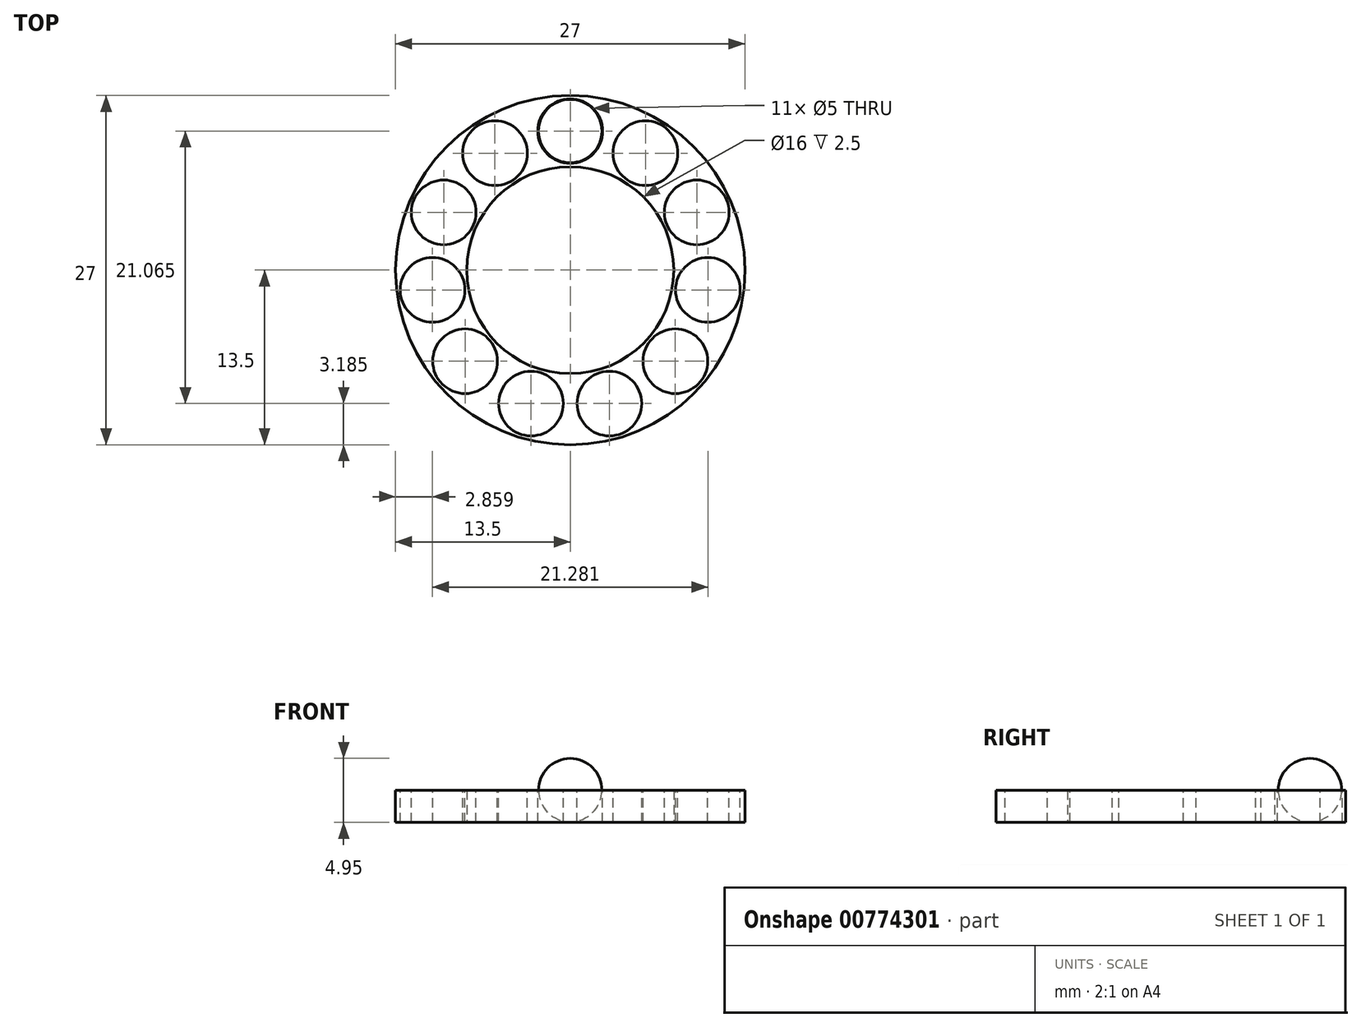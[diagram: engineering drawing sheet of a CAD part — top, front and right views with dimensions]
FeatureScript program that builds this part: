
annotation { "Feature Type Name" : "Feature", "Feature Type Description" : "" }
export const myFeature = defineFeature(function(context is Context, id is Id, definition is map)
    precondition{}
    {
        {
            var Q0;
            Q0=qCreatedBy(makeId("Top.planeOp"),FACE);
            var sketch = newSketch(context, id + "F0", { "sketchPlane" : qUnion([Q0])});
            skCircle(sketch, "E0", {"center": v(0, 0) * mm, "radius": 8 * mm});
            skCircle(sketch, "E1", {"center": v(0, 0) * mm, "radius": 13.5 * mm});
            skSolve(sketch);
        }
        {
            var Q0;
            Q0 = qSketchRegion(id + "F0", true);
            extrude(context, id + "F1", {"entities" : qUnion([Q0]), "depth" : 2.5 * mm, "offsetDistance" : 25 * mm});
        }
        {
            var Q0;
            Q0=makeQuery(id+"F1.opExtrude","CAP_FACE",FACE,{"disambiguationData":[OSD([sQuery(id+"F0.wireOp",EDGE,"E0"),sQuery(id+"F0.wireOp",EDGE,"E1")])],"isStart":false});
            var sketch = newSketch(context, id + "F2", { "sketchPlane" : qUnion([Q0])});
            skCircle(sketch, "E2", {"center": v(0, 10.75) * mm, "radius": 2.5 * mm});
            skCircle(sketch, "E3.1.0", {"center": v(5.81, 9.04) * mm, "radius": 2.5 * mm});
            skCircle(sketch, "E3.2.0", {"center": v(9.78, 4.47) * mm, "radius": 2.5 * mm});
            skCircle(sketch, "E3.3.0", {"center": v(10.64, -1.53) * mm, "radius": 2.5 * mm});
            skCircle(sketch, "E3.4.0", {"center": v(8.12, -7.04) * mm, "radius": 2.5 * mm});
            skCircle(sketch, "E3.5.0", {"center": v(3.03, -10.31) * mm, "radius": 2.5 * mm});
            skCircle(sketch, "E3.6.0", {"center": v(-3.03, -10.31) * mm, "radius": 2.5 * mm});
            skCircle(sketch, "E3.7.0", {"center": v(-8.12, -7.04) * mm, "radius": 2.5 * mm});
            skCircle(sketch, "E3.8.0", {"center": v(-10.64, -1.53) * mm, "radius": 2.5 * mm});
            skCircle(sketch, "E3.9.0", {"center": v(-9.78, 4.47) * mm, "radius": 2.5 * mm});
            skCircle(sketch, "E3.10.0", {"center": v(-5.81, 9.04) * mm, "radius": 2.5 * mm});
            skPoint(sketch, "E3.center", {"position": v(0, 0) * mm});
            skLineSegment(sketch, "E3.anchor1", {"start": v(0, 0) * mm, "end": v(0, 10.75) * mm, "construction": true});
            skLineSegment(sketch, "E3.anchor2", {"start": v(0, 0) * mm, "end": v(-5.81, 9.04) * mm, "construction": true});
            skSolve(sketch);
        }
        {
            var Q0;
            Q0 = qSketchRegion(id + "F2", true);
            extrude(context, id + "F3", {"entities" : qUnion([Q0]), "operationType" : NewBodyOperationType.REMOVE, "oppositeDirection" : true, "depth" : 2.5 * mm, "offsetDistance" : 25 * mm});
        }
        {
            var Q0;
            Q0=makeQuery(id+"F1.opExtrude","CAP_FACE",FACE,{"disambiguationData":[OSD([sQuery(id+"F0.wireOp",EDGE,"E0"),sQuery(id+"F0.wireOp",EDGE,"E1")])],"isStart":false});
            var sketch = newSketch(context, id + "F4", { "sketchPlane" : qUnion([Q0])});
            skLineSegment(sketch, "E4", {"start": v(0, 10.75) * mm, "end": v(2.45, 10.75) * mm});
            skLineSegment(sketch, "E5", {"start": v(0, 10.75) * mm, "end": v(-2.45, 10.75) * mm});
            skArc(sketch, "E6", {"start": v(-2.45, 10.75) * mm, "mid": v(0, 8.3) * mm, "end": v(2.45, 10.75) * mm});
            skSolve(sketch);
        }
        {
            var Q0;
            Q0 = qSketchRegion(id + "F4", true);
            var Q1;
            Q1=sQuery(id+"F4.wireOp",EDGE,"E4");
            revolve(context, id + "F5", {"surfaceOperationType" : NewSurfaceOperationType.NEW, "entities" : qUnion([Q0]), "axis" : qUnion([Q1]), "revolveType" : RevolveType.FULL});
        }
    });
